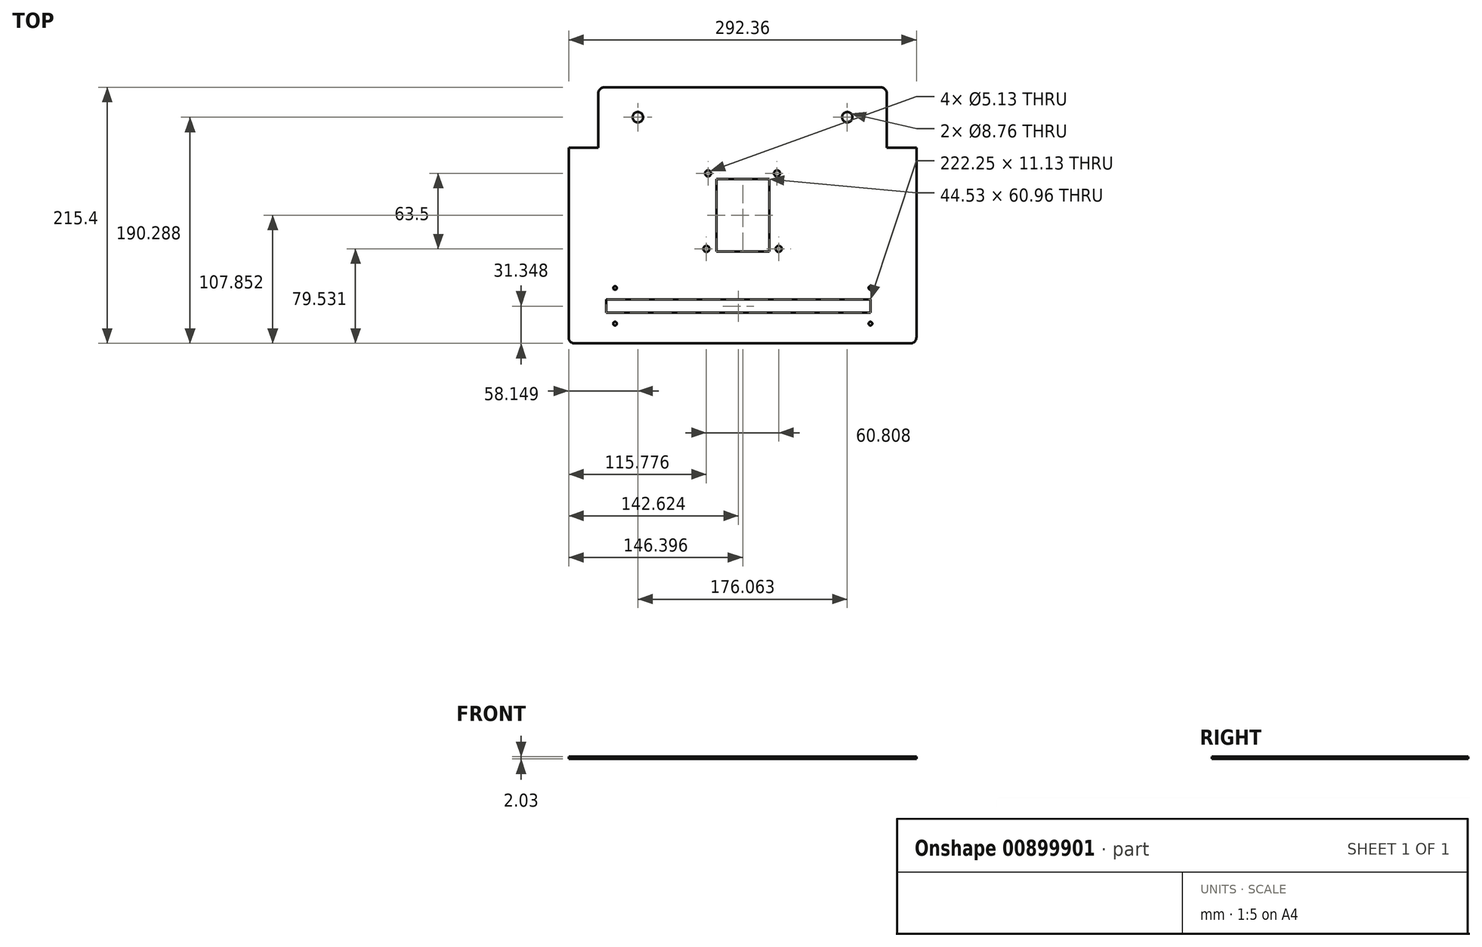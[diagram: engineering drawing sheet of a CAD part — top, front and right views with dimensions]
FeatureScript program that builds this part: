
annotation { "Feature Type Name" : "Feature", "Feature Type Description" : "" }
export const myFeature = defineFeature(function(context is Context, id is Id, definition is map)
    precondition{}
    {
        {
            var Q0;
            Q0=qCreatedBy(makeId("Top.planeOp"),FACE);
            var sketch = newSketch(context, id + "F0", { "sketchPlane" : qUnion([Q0])});
            skLineSegment(sketch, "E0.bottom", {"start": v(-22.05, -4.93) * mm, "end": v(22.48, -4.93) * mm});
            skLineSegment(sketch, "E0.top", {"start": v(-22.05, 56.03) * mm, "end": v(22.48, 56.03) * mm});
            skLineSegment(sketch, "E0.left", {"start": v(-22.05, -4.93) * mm, "end": v(-22.05, 56.03) * mm});
            skLineSegment(sketch, "E0.right", {"start": v(22.48, -4.93) * mm, "end": v(22.48, 56.03) * mm});
            skPoint(sketch, "E0.middle", {"position": v(0, 0) * mm});
            skLineSegment(sketch, "E1.bottom", {"start": v(-146.18, -82.3) * mm, "end": v(146.18, -82.3) * mm});
            skLineSegment(sketch, "E1.top", {"start": v(-146.18, 82.3) * mm, "end": v(-121.29, 82.3) * mm});
            skLineSegment(sketch, "E1.left", {"start": v(-146.18, -82.3) * mm, "end": v(-146.18, 82.3) * mm});
            skLineSegment(sketch, "E1.right", {"start": v(146.18, -82.3) * mm, "end": v(146.18, 82.3) * mm});
            skLineSegment(sketch, "E2", {"start": v(-121.29, 82.3) * mm, "end": v(-121.29, 133.1) * mm});
            skLineSegment(sketch, "E3", {"start": v(-121.29, 133.1) * mm, "end": v(121.29, 133.1) * mm});
            skLineSegment(sketch, "E4", {"start": v(121.29, 133.1) * mm, "end": v(121.29, 82.3) * mm});
            skLineSegment(sketch, "E5.trimOffspring", {"start": v(121.29, 82.3) * mm, "end": v(146.18, 82.3) * mm});
            skLineSegment(sketch, "E6.bottom", {"start": v(-114.68, -56.52) * mm, "end": v(107.57, -56.52) * mm});
            skLineSegment(sketch, "E6.top", {"start": v(-114.68, -45.39) * mm, "end": v(107.57, -45.39) * mm});
            skLineSegment(sketch, "E6.left", {"start": v(-114.68, -56.52) * mm, "end": v(-114.68, -45.39) * mm});
            skLineSegment(sketch, "E6.right", {"start": v(107.57, -56.52) * mm, "end": v(107.57, -45.39) * mm});
            skCircle(sketch, "E7", {"center": v(88.03, 107.99) * mm, "radius": 4.38 * mm});
            skCircle(sketch, "E8.MirrorC", {"center": v(-88.03, 107.99) * mm, "radius": 4.38 * mm});
            skCircle(sketch, "E9", {"center": v(30.4, -2.77) * mm, "radius": 2.57 * mm});
            skCircle(sketch, "E10.MirrorC", {"center": v(-30.4, -2.77) * mm, "radius": 2.57 * mm});
            skCircle(sketch, "E11", {"center": v(29, 60.73) * mm, "radius": 2.57 * mm});
            skCircle(sketch, "E12.MirrorC", {"center": v(-29, 60.73) * mm, "radius": 2.57 * mm});
            skCircle(sketch, "E13", {"center": v(107.57, -65.63) * mm, "radius": 1.52 * mm});
            skCircle(sketch, "E14", {"center": v(107.57, -35.59) * mm, "radius": 1.52 * mm});
            skCircle(sketch, "E15", {"center": v(-107.19, -65.63) * mm, "radius": 1.52 * mm});
            skCircle(sketch, "E16", {"center": v(-107.19, -35.66) * mm, "radius": 1.52 * mm});
            skSolve(sketch);
        }
        {
            var Q0;
            Q0 = qSketchRegion(id + "F0", true);
            extrude(context, id + "F1", {"entities" : qUnion([Q0]), "depth" : 2.03 * mm, "offsetDistance" : 25.4 * mm});
        }
        {
            var Q0;
            Q0=makeQuery(id+"F1.opExtrude","SWEPT_EDGE",EDGE,{"disambiguationData":[OSD([sQuery(id+"F0.wireOp",EDGE,"E3"),sQuery(id+"F0.wireOp",EDGE,"E4")])]});
            var Q1;
            Q1=makeQuery(id+"F1.opExtrude","SWEPT_EDGE",EDGE,{"disambiguationData":[OSD([sQuery(id+"F0.wireOp",EDGE,"E2"),sQuery(id+"F0.wireOp",EDGE,"E3")])]});
            var Q2;
            Q2=makeQuery(id+"F1.opExtrude","SWEPT_EDGE",EDGE,{"disambiguationData":[OSD([sQuery(id+"F0.wireOp",EDGE,"E1.bottom"),sQuery(id+"F0.wireOp",EDGE,"E1.right")])]});
            var Q3;
            Q3=makeQuery(id+"F1.opExtrude","SWEPT_EDGE",EDGE,{"disambiguationData":[OSD([sQuery(id+"F0.wireOp",EDGE,"E1.bottom"),sQuery(id+"F0.wireOp",EDGE,"E1.left")])]});
            fillet(context, id + "F2", {"entities" : qUnion([Q0, Q1, Q2, Q3]), "radius" : 5.08 * mm, "tangentPropagation" : true, "allowEdgeOverflow" : false});
        }
    });
